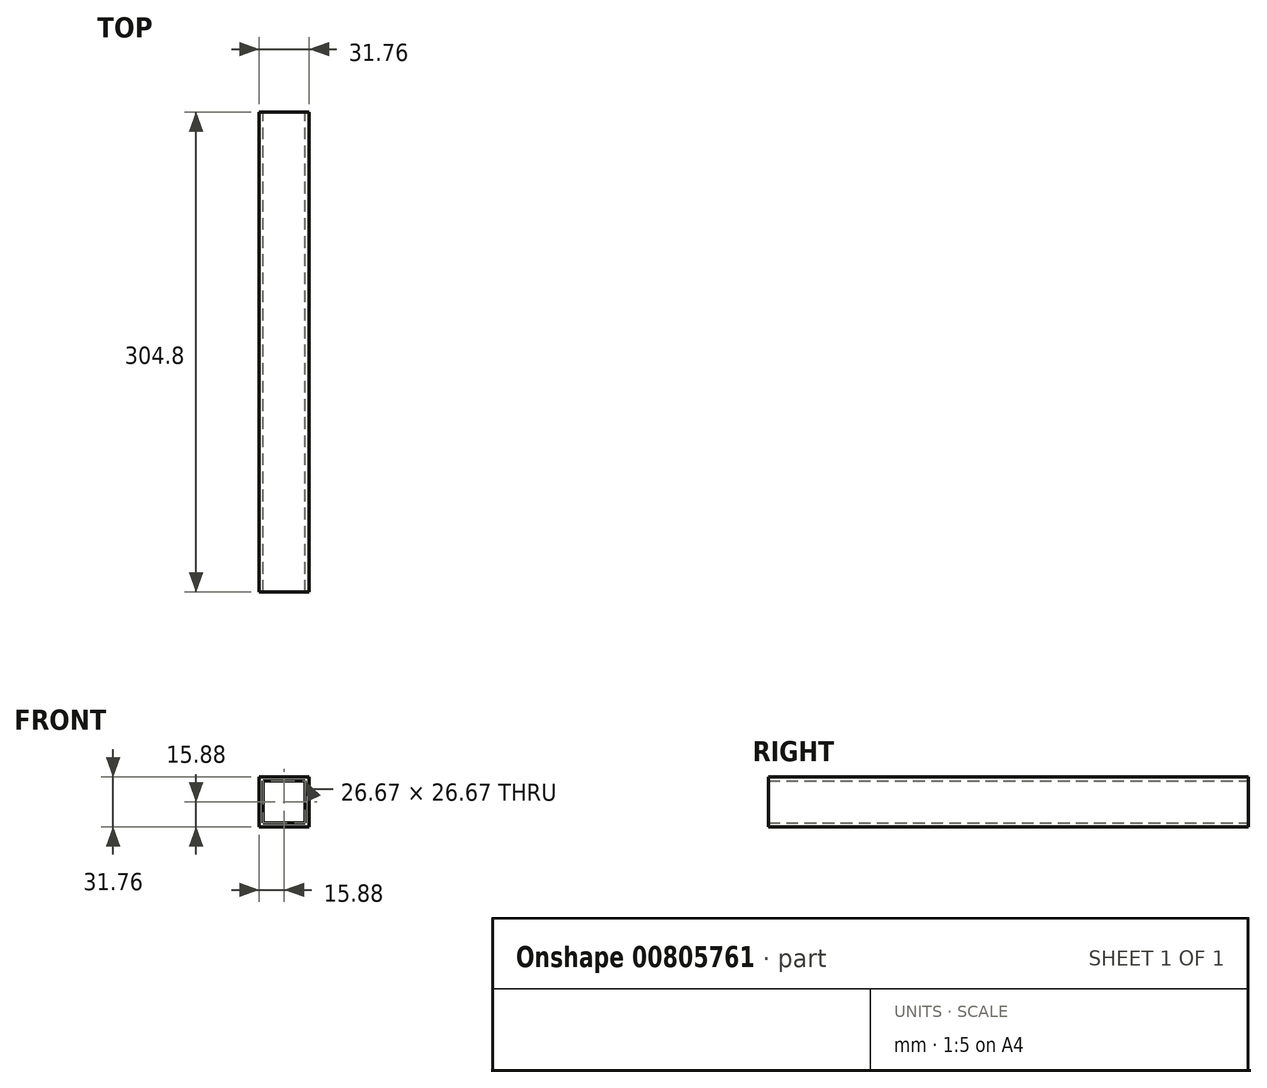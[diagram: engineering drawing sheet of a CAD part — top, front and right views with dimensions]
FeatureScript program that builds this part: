
annotation { "Feature Type Name" : "Feature", "Feature Type Description" : "" }
export const myFeature = defineFeature(function(context is Context, id is Id, definition is map)
    precondition{}
    {
        {
            var Q0;
            Q0=qCreatedBy(makeId("Front.planeOp"),FACE);
            var sketch = newSketch(context, id + "F0", { "sketchPlane" : qUnion([Q0])});
            skLineSegment(sketch, "E0.bottom", {"start": v(15.88, -15.87) * mm, "end": v(-15.87, -15.88) * mm});
            skLineSegment(sketch, "E0.top", {"start": v(15.88, 15.88) * mm, "end": v(-15.87, 15.87) * mm});
            skLineSegment(sketch, "E0.left", {"start": v(15.88, -15.88) * mm, "end": v(15.88, 15.88) * mm});
            skLineSegment(sketch, "E0.right", {"start": v(-15.87, -15.88) * mm, "end": v(-15.87, 15.88) * mm});
            skPoint(sketch, "E0.middle", {"position": v(0, 0) * mm});
            skLineSegment(sketch, "E1.bottom", {"start": v(13.33, -13.33) * mm, "end": v(-13.33, -13.33) * mm});
            skLineSegment(sketch, "E1.top", {"start": v(13.33, 13.33) * mm, "end": v(-13.33, 13.33) * mm});
            skLineSegment(sketch, "E1.left", {"start": v(13.34, -13.33) * mm, "end": v(13.33, 13.33) * mm});
            skLineSegment(sketch, "E1.right", {"start": v(-13.33, -13.33) * mm, "end": v(-13.34, 13.33) * mm});
            skSolve(sketch);
        }
        {
            var Q0;
            Q0=makeQuery(id+"F0.imprint","IMPRINT",FACE,{"disambiguationData":[TD([[makeQuery(id+"F0.imprint","IMPRINT",EDGE,{"derivedFrom":sQuery(id+"F0.wireOp",EDGE,"E0.bottom")}),-1.0]])]});
            extrude(context, id + "F1", {"entities" : qUnion([Q0]), "endBound" : BoundingType.SYMMETRIC, "depth" : 304.8 * mm, "offsetDistance" : 25.4 * mm});
        }
    });
